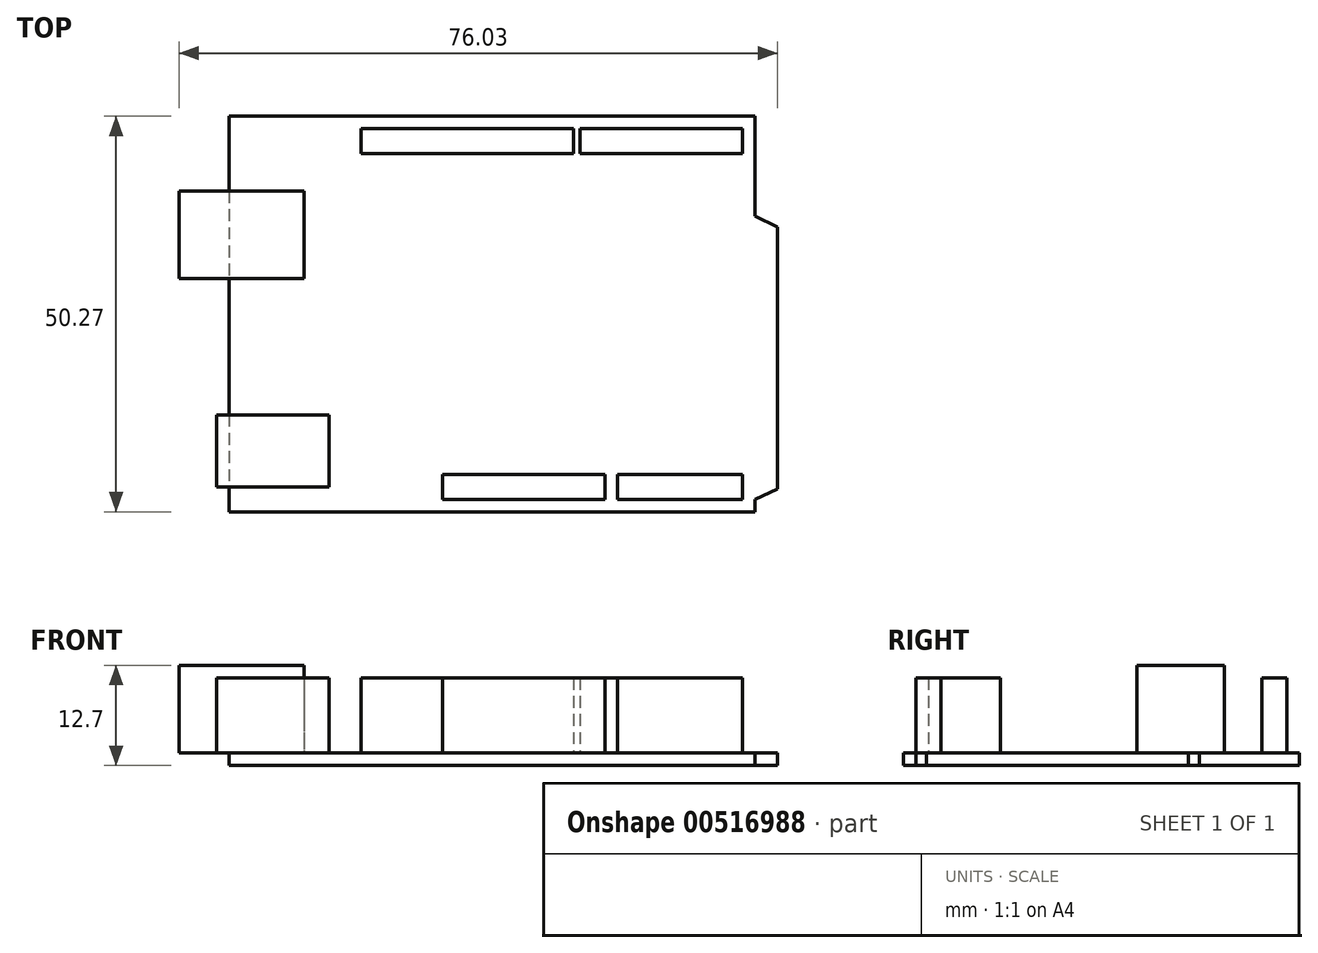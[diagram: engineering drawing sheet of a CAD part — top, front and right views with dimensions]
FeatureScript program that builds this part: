
annotation { "Feature Type Name" : "Feature", "Feature Type Description" : "" }
export const myFeature = defineFeature(function(context is Context, id is Id, definition is map)
    precondition{}
    {
        {
            var Q0;
            Q0=qCreatedBy(makeId("Top.planeOp"),FACE);
            var sketch = newSketch(context, id + "F0", { "sketchPlane" : qUnion([Q0])});
            skLineSegment(sketch, "E0", {"start": v(-38.36, -13.08) * mm, "end": v(28.45, -13.08) * mm});
            skLineSegment(sketch, "E1", {"start": v(28.45, -13.08) * mm, "end": v(28.45, -11.5) * mm});
            skLineSegment(sketch, "E2", {"start": v(28.45, -11.5) * mm, "end": v(31.32, -10.14) * mm});
            skLineSegment(sketch, "E3", {"start": v(31.32, -10.14) * mm, "end": v(31.32, 23.13) * mm});
            skLineSegment(sketch, "E4", {"start": v(31.32, 23.13) * mm, "end": v(28.45, 24.49) * mm});
            skLineSegment(sketch, "E5", {"start": v(28.45, 24.49) * mm, "end": v(28.45, 37.19) * mm});
            skLineSegment(sketch, "E6", {"start": v(28.45, 37.19) * mm, "end": v(-38.36, 37.19) * mm});
            skLineSegment(sketch, "E7", {"start": v(-38.36, 37.19) * mm, "end": v(-38.36, -13.08) * mm});
            skSolve(sketch);
        }
        {
            var Q0;
            Q0 = qSketchRegion(id + "F0", true);
            extrude(context, id + "F1", {"entities" : qUnion([Q0]), "depth" : 1.59 * mm, "offsetDistance" : 25.4 * mm});
        }
        {
            var Q0;
            Q0=makeQuery(id+"F1.opExtrude","CAP_FACE",FACE,{"disambiguationData":[OSD([sQuery(id+"F0.wireOp",EDGE,"E0"),sQuery(id+"F0.wireOp",EDGE,"E1"),sQuery(id+"F0.wireOp",EDGE,"E2"),sQuery(id+"F0.wireOp",EDGE,"E3"),sQuery(id+"F0.wireOp",EDGE,"E4"),sQuery(id+"F0.wireOp",EDGE,"E5"),sQuery(id+"F0.wireOp",EDGE,"E6"),sQuery(id+"F0.wireOp",EDGE,"E7")])],"isStart":false});
            var sketch = newSketch(context, id + "F2", { "sketchPlane" : qUnion([Q0])});
            skLineSegment(sketch, "E8.bottom", {"start": v(-44.7, 27.66) * mm, "end": v(-28.83, 27.66) * mm});
            skLineSegment(sketch, "E8.top", {"start": v(-44.7, 16.55) * mm, "end": v(-28.83, 16.55) * mm});
            skLineSegment(sketch, "E8.left", {"start": v(-44.7, 27.66) * mm, "end": v(-44.7, 16.55) * mm});
            skLineSegment(sketch, "E8.right", {"start": v(-28.83, 27.66) * mm, "end": v(-28.83, 16.55) * mm});
            skPoint(sketch, "E8.middle", {"position": v(-36.77, 22.1) * mm});
            skPoint(sketch, "E9", {"position": v(-38.36, 37.19) * mm});
            skSolve(sketch);
        }
        {
            var Q0;
            Q0 = qSketchRegion(id + "F2", true);
            extrude(context, id + "F3", {"entities" : qUnion([Q0]), "operationType" : NewBodyOperationType.ADD, "depth" : 11.1 * mm, "offsetDistance" : 25.4 * mm});
        }
        {
            var Q0;
            Q0=makeQuery(id+"F1.opExtrude","CAP_FACE",FACE,{"disambiguationData":[OSD([sQuery(id+"F0.wireOp",EDGE,"E0"),sQuery(id+"F0.wireOp",EDGE,"E1"),sQuery(id+"F0.wireOp",EDGE,"E2"),sQuery(id+"F0.wireOp",EDGE,"E3"),sQuery(id+"F0.wireOp",EDGE,"E4"),sQuery(id+"F0.wireOp",EDGE,"E5"),sQuery(id+"F0.wireOp",EDGE,"E6"),sQuery(id+"F0.wireOp",EDGE,"E7")])],"isStart":false});
            var sketch = newSketch(context, id + "F4", { "sketchPlane" : qUnion([Q0])});
            skLineSegment(sketch, "E10.bottom", {"start": v(-39.94, -0.76) * mm, "end": v(-25.66, -0.76) * mm});
            skLineSegment(sketch, "E10.top", {"start": v(-39.94, -9.9) * mm, "end": v(-25.66, -9.9) * mm});
            skLineSegment(sketch, "E10.left", {"start": v(-39.94, -0.76) * mm, "end": v(-39.94, -9.9) * mm});
            skLineSegment(sketch, "E10.right", {"start": v(-25.66, -0.76) * mm, "end": v(-25.66, -9.9) * mm});
            skPoint(sketch, "E10.middle", {"position": v(-32.8, -5.34) * mm});
            skSolve(sketch);
        }
        {
            var Q0;
            {var subQ0=sQuery(id+"F4.wireOp",EDGE,"E10.left");Q0=makeQuery(id+"F4.imprint","IMPRINT",FACE,{"disambiguationData":[TD([[makeQuery(id+"F4.imprint","IMPRINT",EDGE,{"derivedFrom":subQ0}),1.0]])]});}
            var Q1;
            {var subQ0=sQuery(id+"F4.wireOp",EDGE,"E10.right");Q1=makeQuery(id+"F4.imprint","IMPRINT",FACE,{"disambiguationData":[TD([[makeQuery(id+"F4.imprint","IMPRINT",EDGE,{"derivedFrom":subQ0}),-1.0]])]});}
            extrude(context, id + "F5", {"entities" : qUnion([Q0, Q1]), "operationType" : NewBodyOperationType.ADD, "depth" : 9.52 * mm, "offsetDistance" : 25.4 * mm});
        }
        {
            var Q0;
            Q0=makeQuery(id+"F1.opExtrude","CAP_FACE",FACE,{"disambiguationData":[OSD([sQuery(id+"F0.wireOp",EDGE,"E0"),sQuery(id+"F0.wireOp",EDGE,"E1"),sQuery(id+"F0.wireOp",EDGE,"E2"),sQuery(id+"F0.wireOp",EDGE,"E3"),sQuery(id+"F0.wireOp",EDGE,"E4"),sQuery(id+"F0.wireOp",EDGE,"E5"),sQuery(id+"F0.wireOp",EDGE,"E6"),sQuery(id+"F0.wireOp",EDGE,"E7")])],"isStart":false});
            var sketch = newSketch(context, id + "F6", { "sketchPlane" : qUnion([Q0])});
            skLineSegment(sketch, "E11.bottom", {"start": v(9.4, -11.5) * mm, "end": v(-11.24, -11.5) * mm});
            skLineSegment(sketch, "E11.top", {"start": v(9.4, -8.32) * mm, "end": v(-11.24, -8.32) * mm});
            skLineSegment(sketch, "E11.left", {"start": v(9.4, -11.5) * mm, "end": v(9.4, -8.32) * mm});
            skLineSegment(sketch, "E11.right", {"start": v(-11.24, -11.5) * mm, "end": v(-11.24, -8.32) * mm});
            skPoint(sketch, "E11.middle", {"position": v(-0.92, -9.9) * mm});
            skLineSegment(sketch, "E12.bottom", {"start": v(26.86, -11.5) * mm, "end": v(10.98, -11.5) * mm});
            skLineSegment(sketch, "E12.top", {"start": v(26.86, -8.32) * mm, "end": v(10.98, -8.32) * mm});
            skLineSegment(sketch, "E12.left", {"start": v(26.86, -11.5) * mm, "end": v(26.86, -8.32) * mm});
            skLineSegment(sketch, "E12.right", {"start": v(10.98, -11.5) * mm, "end": v(10.98, -8.32) * mm});
            skLineSegment(sketch, "E13.bottom", {"start": v(5.43, 32.42) * mm, "end": v(-21.56, 32.42) * mm});
            skLineSegment(sketch, "E13.top", {"start": v(5.43, 35.6) * mm, "end": v(-21.56, 35.6) * mm});
            skLineSegment(sketch, "E13.left", {"start": v(5.43, 32.42) * mm, "end": v(5.43, 35.6) * mm});
            skLineSegment(sketch, "E13.right", {"start": v(-21.56, 32.42) * mm, "end": v(-21.56, 35.6) * mm});
            skLineSegment(sketch, "E14.bottom", {"start": v(26.86, 32.42) * mm, "end": v(6.22, 32.42) * mm});
            skLineSegment(sketch, "E14.top", {"start": v(26.86, 35.6) * mm, "end": v(6.22, 35.6) * mm});
            skLineSegment(sketch, "E14.left", {"start": v(26.86, 32.42) * mm, "end": v(26.86, 35.6) * mm});
            skLineSegment(sketch, "E14.right", {"start": v(6.22, 32.42) * mm, "end": v(6.22, 35.6) * mm});
            skSolve(sketch);
        }
        {
            var Q0;
            Q0=makeQuery(id+"F6.imprint","IMPRINT",FACE,{"disambiguationData":[TD([[makeQuery(id+"F6.imprint","IMPRINT",EDGE,{"derivedFrom":sQuery(id+"F6.wireOp",EDGE,"E13.bottom")}),-1.0]])]});
            var Q1;
            Q1=makeQuery(id+"F6.imprint","IMPRINT",FACE,{"disambiguationData":[TD([[makeQuery(id+"F6.imprint","IMPRINT",EDGE,{"derivedFrom":sQuery(id+"F6.wireOp",EDGE,"E14.bottom")}),-1.0]])]});
            var Q2;
            Q2=makeQuery(id+"F6.imprint","IMPRINT",FACE,{"disambiguationData":[TD([[makeQuery(id+"F6.imprint","IMPRINT",EDGE,{"derivedFrom":sQuery(id+"F6.wireOp",EDGE,"E11.bottom")}),-1.0]])]});
            var Q3;
            Q3=makeQuery(id+"F6.imprint","IMPRINT",FACE,{"disambiguationData":[TD([[makeQuery(id+"F6.imprint","IMPRINT",EDGE,{"derivedFrom":sQuery(id+"F6.wireOp",EDGE,"E12.bottom")}),-1.0]])]});
            extrude(context, id + "F7", {"entities" : qUnion([Q0, Q1, Q2, Q3]), "operationType" : NewBodyOperationType.ADD, "depth" : 9.52 * mm, "offsetDistance" : 25.4 * mm});
        }
    });
